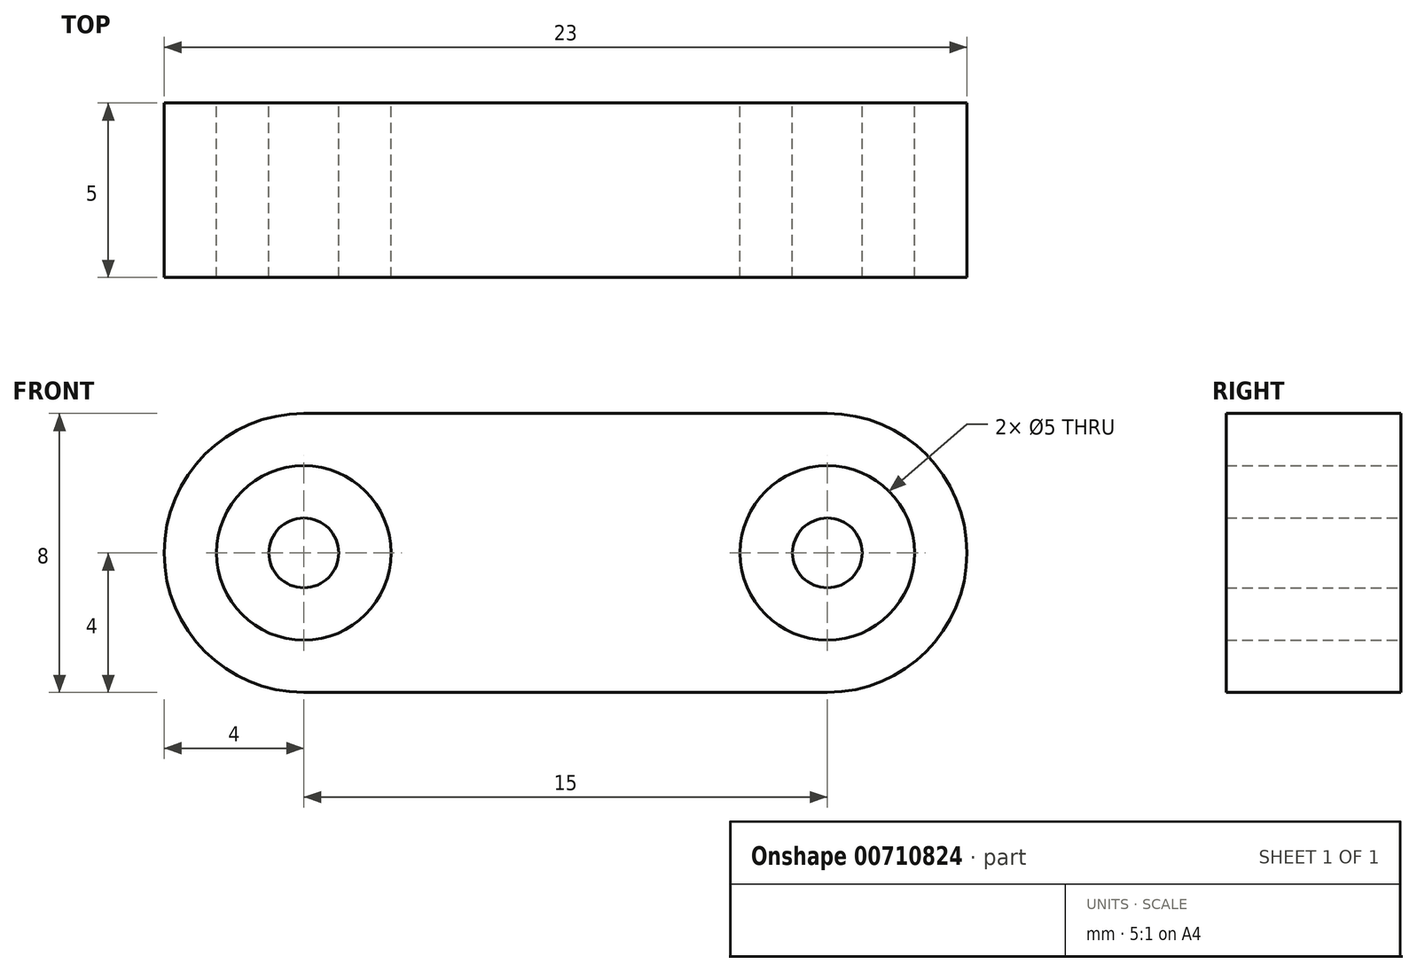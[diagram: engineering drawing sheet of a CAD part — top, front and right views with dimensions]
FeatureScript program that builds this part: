
annotation { "Feature Type Name" : "Feature", "Feature Type Description" : "" }
export const myFeature = defineFeature(function(context is Context, id is Id, definition is map)
    precondition{}
    {
        {
            var Q0;
            Q0=qCreatedBy(makeId("Front.planeOp"),FACE);
            var sketch = newSketch(context, id + "F0", { "sketchPlane" : qUnion([Q0])});
            skCircle(sketch, "E0", {"center": v(0, 0) * mm, "radius": 2.5 * mm});
            skCircle(sketch, "E1", {"center": v(0, 0) * mm, "radius": 1 * mm});
            skArc(sketch, "E2", {"start": v(0, 4) * mm, "mid": v(-4, 0) * mm, "end": v(0, -4) * mm});
            skCircle(sketch, "E3", {"center": v(15, 0) * mm, "radius": 1 * mm});
            skCircle(sketch, "E4", {"center": v(15, 0) * mm, "radius": 2.5 * mm});
            skArc(sketch, "E5", {"start": v(15, -4) * mm, "mid": v(19, 0) * mm, "end": v(15, 4) * mm});
            skLineSegment(sketch, "E6", {"start": v(0, 4) * mm, "end": v(15, 4) * mm});
            skLineSegment(sketch, "E7", {"start": v(0, -4) * mm, "end": v(15, -4) * mm});
            skSolve(sketch);
        }
        {
            var Q0;
            Q0=makeQuery(id+"F0.imprint","IMPRINT",FACE,{"disambiguationData":[TD([[makeQuery(id+"F0.imprint","IMPRINT",EDGE,{"derivedFrom":sQuery(id+"F0.wireOp",EDGE,"E0")}),-1.0]])]});
            var Q1;
            Q1=makeQuery(id+"F0.imprint","IMPRINT",FACE,{"disambiguationData":[TD([[makeQuery(id+"F0.imprint","IMPRINT",EDGE,{"derivedFrom":sQuery(id+"F0.wireOp",EDGE,"E1")}),1.0]])]});
            var Q2;
            Q2=makeQuery(id+"F0.imprint","IMPRINT",FACE,{"disambiguationData":[TD([[makeQuery(id+"F0.imprint","IMPRINT",EDGE,{"derivedFrom":sQuery(id+"F0.wireOp",EDGE,"E3")}),1.0]])]});
            extrude(context, id + "F1", {"entities" : qUnion([Q0, Q1, Q2]), "depth" : 5 * mm, "offsetDistance" : 25 * mm});
        }
    });
